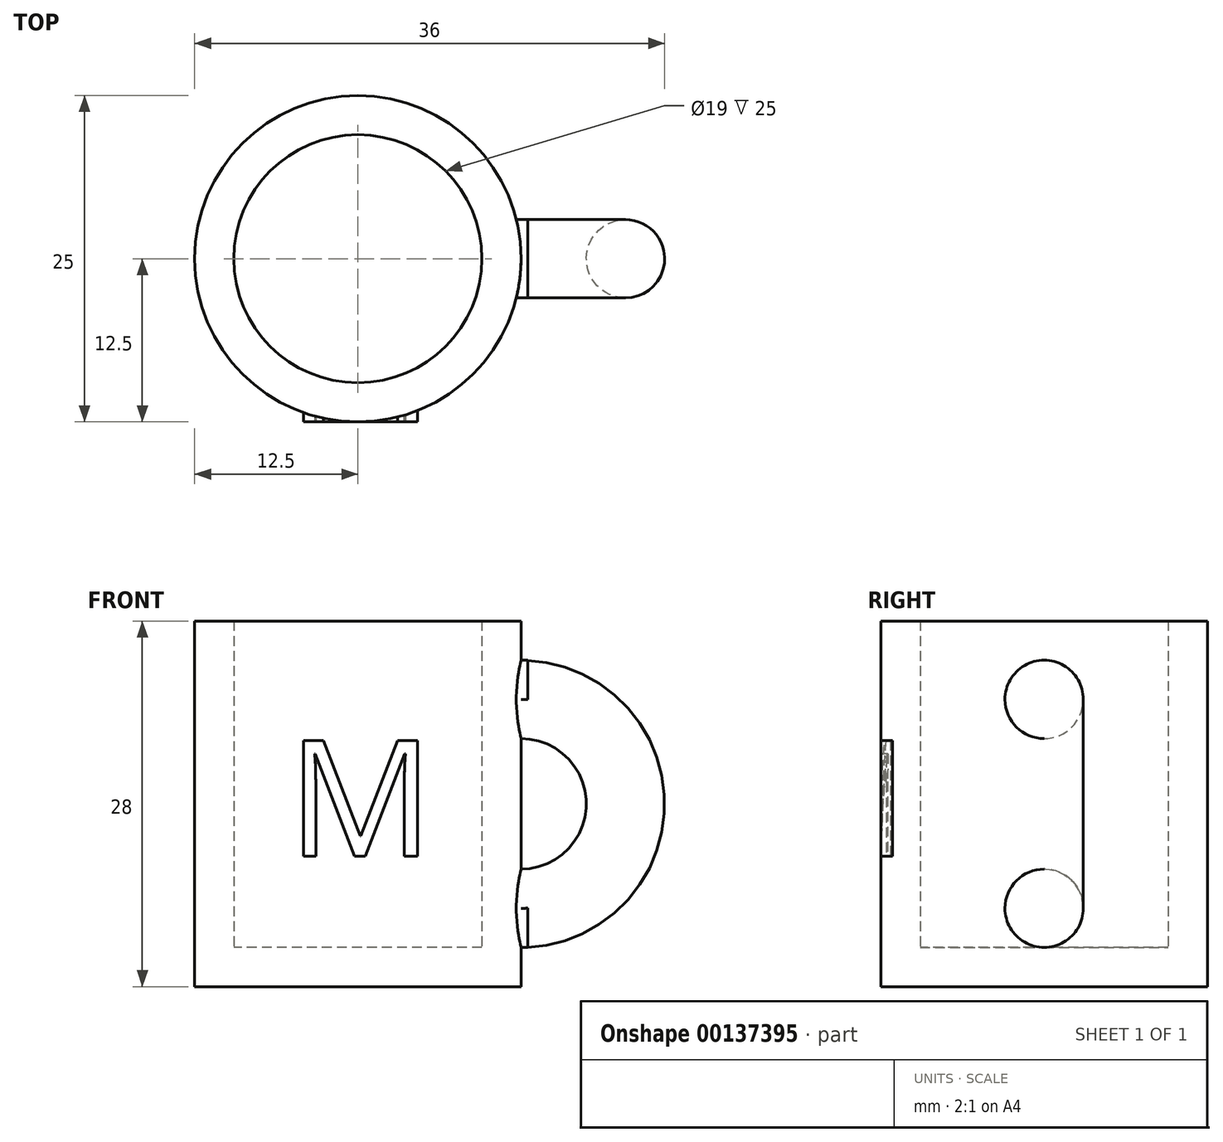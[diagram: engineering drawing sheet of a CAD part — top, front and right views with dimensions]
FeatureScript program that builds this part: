
annotation { "Feature Type Name" : "Feature", "Feature Type Description" : "" }
export const myFeature = defineFeature(function(context is Context, id is Id, definition is map)
    precondition{}
    {
        {
            var Q0;
            Q0=qCreatedBy(makeId("Top.planeOp"),FACE);
            var sketch = newSketch(context, id + "F0", { "sketchPlane" : qUnion([Q0])});
            skCircle(sketch, "E0", {"center": v(0, 0) * mm, "radius": 12.5 * mm});
            skSolve(sketch);
        }
        {
            var Q0;
            Q0 = qSketchRegion(id + "F0", true);
            extrude(context, id + "F1", {"entities" : qUnion([Q0]), "depth" : 3 * mm});
        }
        {
            var Q0;
            Q0=makeQuery(id+"F1.opExtrude","CAP_FACE",FACE,{"disambiguationData":[OSD([sQuery(id+"F0.wireOp",EDGE,"E0")])],"isStart":false});
            var sketch = newSketch(context, id + "F2", { "sketchPlane" : qUnion([Q0])});
            skCircle(sketch, "E1", {"center": v(0, 0) * mm, "radius": 12.5 * mm});
            skCircle(sketch, "E2", {"center": v(0, 0) * mm, "radius": 9.5 * mm});
            skSolve(sketch);
        }
        {
            var Q0;
            Q0 = qSketchRegion(id + "F2", true);
            extrude(context, id + "F3", {"entities" : qUnion([Q0]), "operationType" : NewBodyOperationType.ADD, "depth" : 25 * mm});
        }
        {
            var Q0;
            Q0=qCreatedBy(makeId("Right.planeOp"),FACE);
            cPlane(context, id + "F4", {"entities" : qUnion([Q0]), "cplaneType" : CPlaneType.OFFSET, "offset" : 12.5 * mm, "width" : 150 * mm, "height" : 150 * mm});
        }
        {
            var Q0;
            Q0=qCreatedBy(id+"F4.planeOp",FACE);
            var sketch = newSketch(context, id + "F5", { "sketchPlane" : qUnion([Q0])});
            skCircle(sketch, "E3", {"center": v(0, 22) * mm, "radius": 3 * mm});
            skCircle(sketch, "E4", {"center": v(0, 6) * mm, "radius": 3 * mm});
            skSolve(sketch);
        }
        {
            var Q0;
            Q0 = qSketchRegion(id + "F5", true);
            var Q1;
            Q1=makeQuery(id+"F3.boolean.opBoolean","MERGE",FACE,{"derivedFrom":[makeQuery(id+"F1.opExtrude","SWEPT_FACE",FACE,{"disambiguationData":[OSD([sQuery(id+"F0.wireOp",EDGE,"E0")])]}),makeQuery(id+"F3.opExtrude","SWEPT_FACE",FACE,{"disambiguationData":[OSD([sQuery(id+"F2.wireOp",EDGE,"E1")])]})]});
            extrude(context, id + "F6", {"entities" : qUnion([Q0]), "operationType" : NewBodyOperationType.ADD, "oppositeDirection" : true, "endBoundEntityFace" : qUnion([Q1]), "depth" : 1 * mm});
        }
        {
            var Q0;
            Q0=qCreatedBy(makeId("Front.planeOp"),FACE);
            var sketch = newSketch(context, id + "F7", { "sketchPlane" : qUnion([Q0])});
            skArc(sketch, "E5", {"start": v(12.5, 6) * mm, "mid": v(20.5, 14) * mm, "end": v(12.5, 22) * mm});
            skSolve(sketch);
        }
        {
            var Q0;
            Q0 = qSketchRegion(id + "F5", true);
            var Q1;
            Q1=sQuery(id+"F5.wireOp",EDGE,"E3");
            var Q2;
            Q2 = qConstructionFilter(qBodyType(qCreatedBy(id + "F7" ,EDGE), BodyType.WIRE), ConstructionObject.NO);
            sweep(context, id + "F8", {"profiles" : qUnion([Q0]), "surfaceProfiles" : qUnion([Q1]), "path" : qUnion([Q2])});
        }
        {
            var Q0;
            Q0 = qSketchRegion(id + "F5", true);
            extrude(context, id + "F9", {"entities" : qUnion([Q0]), "operationType" : NewBodyOperationType.ADD, "depth" : .5 * mm});
        }
        {
            var Q0;
            Q0=qCreatedBy(makeId("Front.planeOp"),FACE);
            cPlane(context, id + "F10", {"entities" : qUnion([Q0]), "cplaneType" : CPlaneType.OFFSET, "offset" : 12.5 * mm, "width" : 150 * mm, "height" : 150 * mm});
        }
        {
            var Q0;
            Q0=qCreatedBy(id+"F10.planeOp",FACE);
            var sketch = newSketch(context, id + "F11", { "sketchPlane" : qUnion([Q0])});
            skText(sketch, "E6", { "text": "M", "fontName": "OpenSans-Regular.ttf"});
            const initialGuessF11  = {"E6": [-0.00539, 0.01, 1, 0, 0.00892]};
            skSetInitialGuess(sketch, initialGuessF11);
            skSolve(sketch);
        }
        {
            var Q0;
            Q0 = qSketchRegion(id + "F11", true);
            var Q1;
            Q1=makeQuery(id+"F3.boolean.opBoolean","MERGE",FACE,{"derivedFrom":[makeQuery(id+"F1.opExtrude","SWEPT_FACE",FACE,{"disambiguationData":[OSD([sQuery(id+"F0.wireOp",EDGE,"E0")])]}),makeQuery(id+"F3.opExtrude","SWEPT_FACE",FACE,{"disambiguationData":[OSD([sQuery(id+"F2.wireOp",EDGE,"E1")])]})]});
            extrude(context, id + "F12", {"entities" : qUnion([Q0]), "operationType" : NewBodyOperationType.ADD, "oppositeDirection" : true, "endBoundEntityFace" : qUnion([Q1]), "depth" : 1 * mm});
        }
        {
            var Q0;
            Q0=makeQuery(id+"F3.opExtrude","CAP_FACE",FACE,{"disambiguationData":[OSD([sQuery(id+"F2.wireOp",EDGE,"E1"),sQuery(id+"F2.wireOp",EDGE,"E2")])],"isStart":false});
            var sketch = newSketch(context, id + "F13", { "sketchPlane" : qUnion([Q0])});
            skCircle(sketch, "E7", {"center": v(0, 0) * mm, "radius": 9.5 * mm});
            skSolve(sketch);
        }
        {
            var Q0;
            Q0 = qSketchRegion(id + "F13", true);
            extrude(context, id + "F14", {"entities" : qUnion([Q0]), "operationType" : NewBodyOperationType.REMOVE, "endBound" : BoundingType.UP_TO_NEXT, "oppositeDirection" : true, "depth" : 25 * mm});
        }
    });
